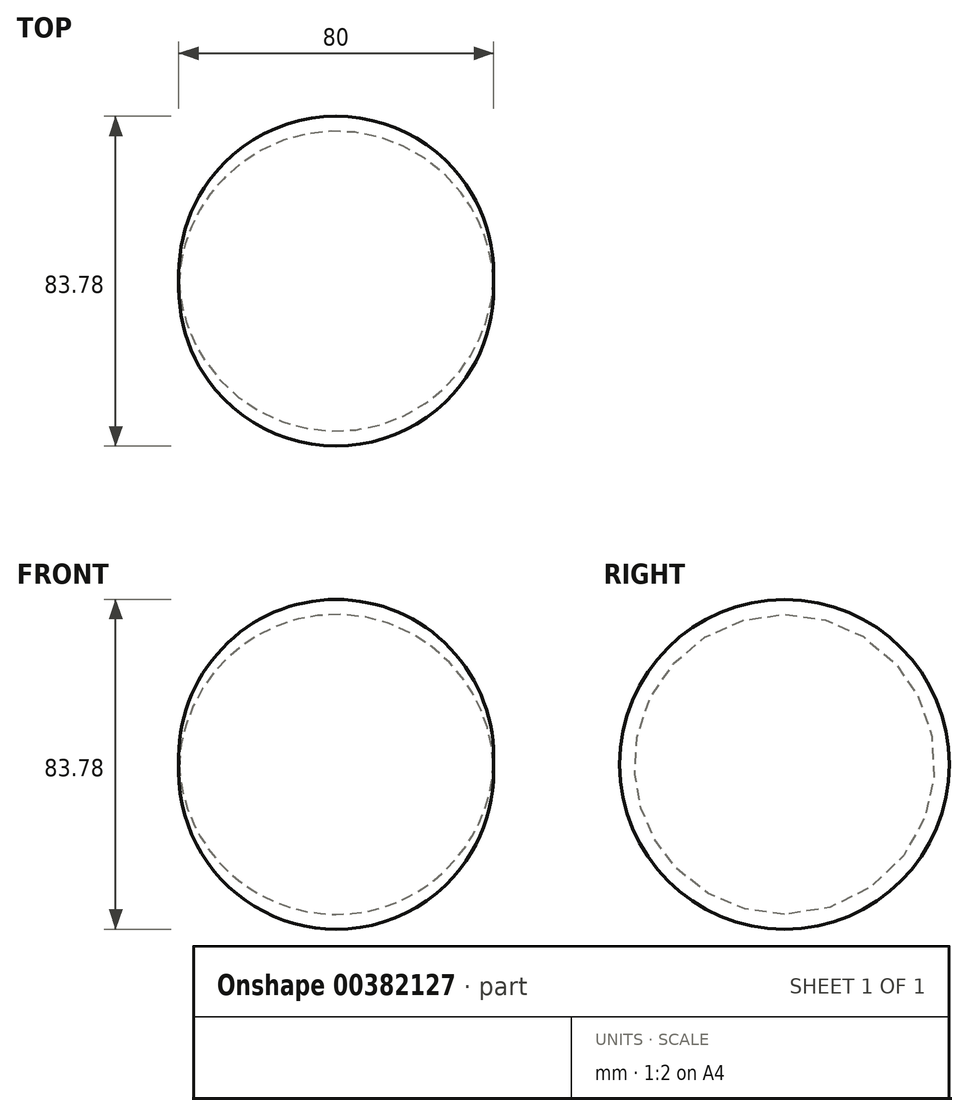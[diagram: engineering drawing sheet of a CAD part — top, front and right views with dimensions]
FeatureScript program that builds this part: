
annotation { "Feature Type Name" : "Feature", "Feature Type Description" : "" }
export const myFeature = defineFeature(function(context is Context, id is Id, definition is map)
    precondition{}
    {
        {
            var Q0;
            Q0=qCreatedBy(makeId("Front.planeOp"),FACE);
            var sketch = newSketch(context, id + "F0", { "sketchPlane" : qUnion([Q0])});
            skLineSegment(sketch, "E0", {"start": v(-39.64, 0) * mm, "end": v(40.27, 0) * mm, "construction": true});
            skArc(sketch, "E1", {"start": v(40.27, 0) * mm, "mid": v(0.32, 38.1) * mm, "end": v(-39.64, 0) * mm});
            skLineSegment(sketch, "E2", {"start": v(-39.64, 0) * mm, "end": v(40.27, 0) * mm});
            skSolve(sketch);
        }
        {
            var Q0;
            Q0 = qSketchRegion(id + "F0", true);
            var Q1;
            Q1=sQuery(id+"F0.wireOp",EDGE,"E2");
            revolve(context, id + "F1", {"entities" : qUnion([Q0]), "axis" : qUnion([Q1]), "revolveType" : RevolveType.FULL});
        }
    });
